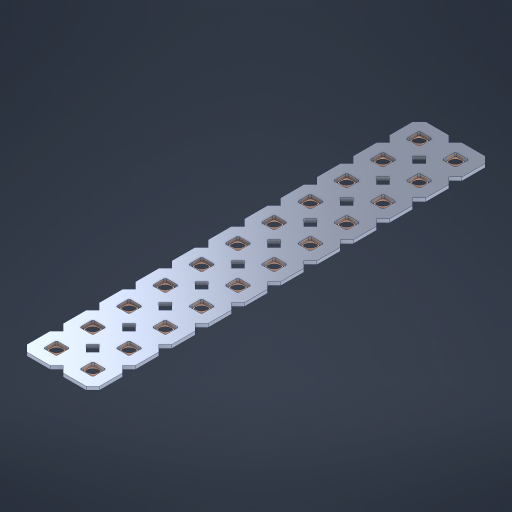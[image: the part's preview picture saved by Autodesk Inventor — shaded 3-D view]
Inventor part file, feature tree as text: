
AUTODESK INVENTOR PART (.ipt)
format: ipt  version: 2023 (Build 270158000, 158)  size: 503,808 bytes
history: native  units: in
note: dims shown in document units (in); Inventor stores cm internally (conversion verified against a paired STEP export)
features: other x23, extrude x21, sketch x2, pattern_linear x1
ambient origin geometry x8: Origin, YZ Plane, XZ Plane, XY Plane, X Axis, Y Axis, Z Axis, Center Point
bodies: Solid1 (feature_tree), Body (feature_tree)
feature tree (47):
  pattern_linear  "Rectangular Pattern1"  Spacing1=0.09in  [1 undecoded]
  sketch  "Sketch1"  dims[d1=0.5in]
  sketch  "Sketch2"  dims[d2=0.182in d3=0.09in d4=0.09in d5=0.09in d6=0.09in d7=0.09in d8=0.09in d9=0.09in d10=0.09in d11=0.02in d13=0.0in d14=0.172in d15=0.0625in d16=0.0in d19=0.5in d22=0.5in]
  other  "Srf1"
  other  "Srf126"
  other  "Srf127"
  other  "Srf128"
  other  "Srf129"
  other  "Srf130"
  other  "Srf131"
  other  "Srf250"
  other  "Srf251"
  other  "Srf252"
  other  "Srf253"
  other  "Srf268"
  other  "Srf269"
  other  "Srf270"
  other  "Srf271"
  other  "Srf272"
  other  "Srf273"
  other  "Srf274"
  other  "Srf275"
  other  "Srf276"
  other  "Srf277"
  other  "Srf278"
  other  "Circle"
  extrude  "ExtrusionSrf126"  Depth=0.09in
  extrude  "ExtrusionSrf127"  Depth=0.09in
  extrude  "ExtrusionSrf128"  Depth=0.09in
  extrude  "ExtrusionSrf129"  Depth=0.09in
  extrude  "ExtrusionSrf130"  Depth=0.09in
  extrude  "ExtrusionSrf131"  Depth=0.09in
  extrude  "ExtrusionSrf250"  Depth=0.09in
  extrude  "ExtrusionSrf251"  Depth=0.02in
  extrude  "ExtrusionSrf252"  TaperAngle=0.0deg  [1 undecoded]
  extrude  "ExtrusionSrf253"  Depth=0.5in
  extrude  "ExtrusionSrf268"  Depth=0.5in TaperAngle=0.0deg
  extrude  "ExtrusionSrf269"  Depth=0.5in
  extrude  "ExtrusionSrf270"  Depth=0.5in
  extrude  "ExtrusionSrf271"  [1 undecoded]
  extrude  "ExtrusionSrf272"  [1 undecoded]
  extrude  "ExtrusionSrf273"  [1 undecoded]
  extrude  "ExtrusionSrf274"  [1 undecoded]
  extrude  "ExtrusionSrf275"  [1 undecoded]
  extrude  "ExtrusionSrf276"  [1 undecoded]
  extrude  "ExtrusionSrf277"  [1 undecoded]
  extrude  "ExtrusionSrf278"  [1 undecoded]
note: 10 required parameter values undecoded (feature->parameter linkage not recoverable at this tier; creation-order binding heuristic only, values carry confidence <= 0.55)
